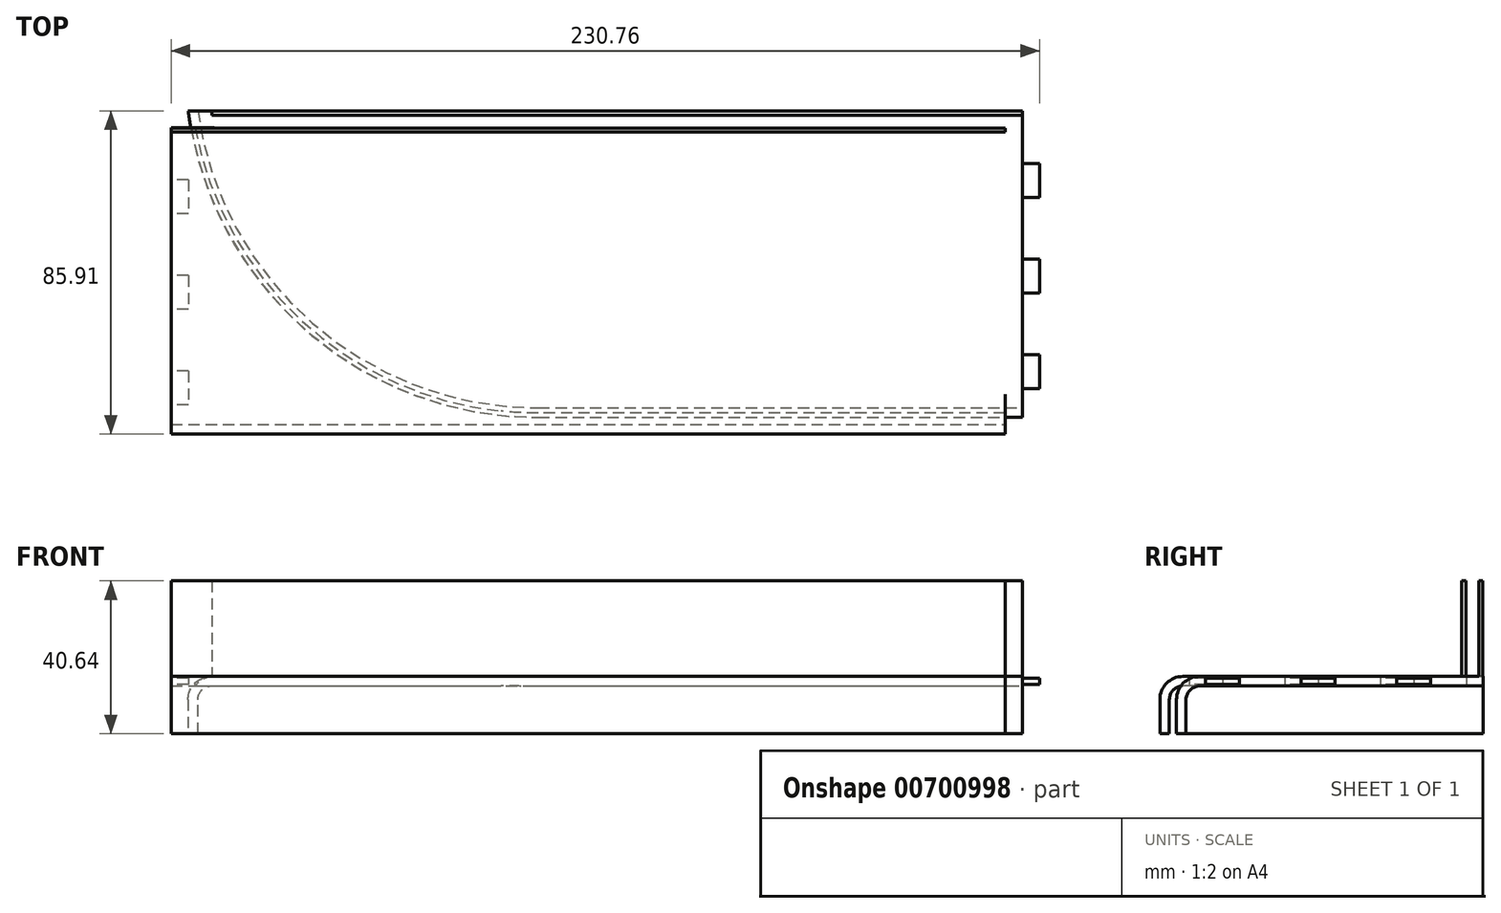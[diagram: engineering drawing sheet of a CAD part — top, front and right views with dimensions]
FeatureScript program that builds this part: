
annotation { "Feature Type Name" : "Feature", "Feature Type Description" : "" }
export const myFeature = defineFeature(function(context is Context, id is Id, definition is map)
    precondition{}
    {
        {
            var Q0;
            Q0=qCreatedBy(makeId("Top.planeOp"),FACE);
            var sketch = newSketch(context, id + "F0", { "sketchPlane" : qUnion([Q0])});
            skLineSegment(sketch, "E0.bottom", {"start": v(-106.27, 45.17) * mm, "end": v(115.37, 45.17) * mm});
            skLineSegment(sketch, "E0.top", {"start": v(-106.27, -36.31) * mm, "end": v(115.37, -36.31) * mm});
            skLineSegment(sketch, "E0.left", {"start": v(-106.27, 45.17) * mm, "end": v(-106.27, -36.31) * mm});
            skLineSegment(sketch, "E0.right", {"start": v(115.37, 45.17) * mm, "end": v(115.37, -36.31) * mm});
            skSolve(sketch);
        }
        {
            var Q0;
            Q0 = qSketchRegion(id + "F0", true);
            extrude(context, id + "F1", {"entities" : qUnion([Q0]), "depth" : 15.24 * mm, "offsetDistance" : 25.4 * mm});
        }
        {
            var Q0;
            Q0=makeQuery(id+"F1.opExtrude","SWEPT_EDGE",EDGE,{"disambiguationData":[OSD([sQuery(id+"F0.wireOp",EDGE,"E0.top"),sQuery(id+"F0.wireOp",EDGE,"E0.left")])]});
            fillet(context, id + "F2", {"entities" : qUnion([Q0]), "radius" : 93.82 * mm, "tangentPropagation" : true, "allowEdgeOverflow" : false});
        }
        {
            var Q0;
            {var subQ0=sQuery(id+"F0.wireOp",EDGE,"E0.left");var subQ1=sQuery(id+"F0.wireOp",EDGE,"E0.bottom");Q0=makeQuery(id+"F2.opFillet","BLEND_EDGE",EDGE,{"blendedFrom":[makeQuery(id+"F1.opExtrude","SWEPT_EDGE",EDGE,{"disambiguationData":[OSD([subQ1,subQ0])]}),makeQuery(id+"F1.opExtrude","CAP_FACE",FACE,{"disambiguationData":[OSD([subQ1,sQuery(id+"F0.wireOp",EDGE,"E0.top"),subQ0,sQuery(id+"F0.wireOp",EDGE,"E0.right")])],"isStart":false})],"blendedInto":[makeQuery(id+"F1.opExtrude","CAP_FACE",FACE,{"disambiguationData":[OSD([subQ1,sQuery(id+"F0.wireOp",EDGE,"E0.top"),subQ0,sQuery(id+"F0.wireOp",EDGE,"E0.right")])],"isStart":false})]});}
            var Q1;
            Q1=makeQuery(id+"F1.opExtrude","CAP_EDGE",EDGE,{"disambiguationData":[OSD([sQuery(id+"F0.wireOp",EDGE,"E0.top")])],"isStart":false});
            fillet(context, id + "F3", {"entities" : qUnion([Q0, Q1]), "radius" : 6.13 * mm, "tangentPropagation" : true, "allowEdgeOverflow" : false});
        }
        {
            var Q0;
            Q0=makeQuery(id+"F1.opExtrude","CAP_FACE",FACE,{"disambiguationData":[OSD([sQuery(id+"F0.wireOp",EDGE,"E0.bottom"),sQuery(id+"F0.wireOp",EDGE,"E0.top"),sQuery(id+"F0.wireOp",EDGE,"E0.left"),sQuery(id+"F0.wireOp",EDGE,"E0.right")])],"isStart":true});
            var Q1;
            Q1=makeQuery(id+"F1.opExtrude","SWEPT_FACE",FACE,{"disambiguationData":[OSD([sQuery(id+"F0.wireOp",EDGE,"E0.bottom")])]});
            var Q2;
            Q2=makeQuery(id+"F1.opExtrude","SWEPT_FACE",FACE,{"disambiguationData":[OSD([sQuery(id+"F0.wireOp",EDGE,"E0.right")])]});
            shell(context, id + "F4", {"entities" : qUnion([Q0, Q1, Q2]), "thickness" : 2.54 * mm});
        }
        {
            var Q0;
            Q0=makeQuery(id+"F1.opExtrude","SWEPT_FACE",FACE,{"disambiguationData":[OSD([sQuery(id+"F0.wireOp",EDGE,"E0.right")])]});
            var sketch = newSketch(context, id + "F5", { "sketchPlane" : qUnion([Q0])});
            skLineSegment(sketch, "E1.bottom", {"start": v(-29.1, 15.24) * mm, "end": v(-19.17, 15.24) * mm});
            skLineSegment(sketch, "E1.top", {"start": v(-29.1, 12.7) * mm, "end": v(-19.17, 12.7) * mm});
            skLineSegment(sketch, "E1.left", {"start": v(-29.1, 15.24) * mm, "end": v(-29.1, 12.7) * mm});
            skLineSegment(sketch, "E1.right", {"start": v(-19.17, 15.24) * mm, "end": v(-19.17, 12.7) * mm});
            skLineSegment(sketch, "E2.1.0.0", {"start": v(-3.7, 15.24) * mm, "end": v(-3.7, 12.7) * mm});
            skLineSegment(sketch, "E2.1.0.1", {"start": v(-3.7, 15.24) * mm, "end": v(6.23, 15.24) * mm});
            skLineSegment(sketch, "E2.1.0.2", {"start": v(-3.7, 12.7) * mm, "end": v(6.23, 12.7) * mm});
            skLineSegment(sketch, "E2.1.0.3", {"start": v(6.23, 15.24) * mm, "end": v(6.23, 12.7) * mm});
            skLineSegment(sketch, "E2.2.0.0", {"start": v(21.7, 15.24) * mm, "end": v(21.7, 12.7) * mm});
            skLineSegment(sketch, "E2.2.0.1", {"start": v(21.7, 15.24) * mm, "end": v(31.63, 15.24) * mm});
            skLineSegment(sketch, "E2.2.0.2", {"start": v(21.7, 12.7) * mm, "end": v(31.63, 12.7) * mm});
            skLineSegment(sketch, "E2.2.0.3", {"start": v(31.63, 15.24) * mm, "end": v(31.63, 12.7) * mm});
            skLineSegment(sketch, "E2.direction1", {"start": v(-29.1, 12.7) * mm, "end": v(-3.7, 12.7) * mm, "construction": true});
            skLineSegment(sketch, "E3.0", {"start": v(-28.6, 14.76) * mm, "end": v(-28.6, 13.18) * mm});
            skLineSegment(sketch, "E3.1", {"start": v(-28.6, 14.76) * mm, "end": v(-19.65, 14.76) * mm});
            skLineSegment(sketch, "E3.2", {"start": v(-19.65, 14.76) * mm, "end": v(-19.65, 13.18) * mm});
            skLineSegment(sketch, "E3.3", {"start": v(-28.6, 13.18) * mm, "end": v(-19.65, 13.18) * mm});
            skLineSegment(sketch, "E4.0", {"start": v(-3.2, 14.76) * mm, "end": v(5.75, 14.76) * mm});
            skLineSegment(sketch, "E4.1", {"start": v(-3.2, 14.76) * mm, "end": v(-3.2, 13.18) * mm});
            skLineSegment(sketch, "E4.2", {"start": v(-3.2, 13.18) * mm, "end": v(5.75, 13.18) * mm});
            skLineSegment(sketch, "E4.3", {"start": v(5.75, 14.76) * mm, "end": v(5.75, 13.18) * mm});
            skLineSegment(sketch, "E5.0", {"start": v(22.2, 14.76) * mm, "end": v(22.2, 13.18) * mm});
            skLineSegment(sketch, "E5.1", {"start": v(22.2, 14.76) * mm, "end": v(31.15, 14.76) * mm});
            skLineSegment(sketch, "E5.2", {"start": v(31.15, 14.76) * mm, "end": v(31.15, 13.18) * mm});
            skLineSegment(sketch, "E5.3", {"start": v(22.2, 13.18) * mm, "end": v(31.15, 13.18) * mm});
            skSolve(sketch);
        }
        {
            var Q0;
            Q0=makeQuery(id+"F5.imprint","IMPRINT",FACE,{"disambiguationData":[TD([[makeQuery(id+"F5.imprint","IMPRINT",EDGE,{"derivedFrom":sQuery(id+"F5.wireOp",EDGE,"E3.0")}),1.0]])]});
            var Q1;
            Q1=makeQuery(id+"F5.imprint","IMPRINT",FACE,{"disambiguationData":[TD([[makeQuery(id+"F5.imprint","IMPRINT",EDGE,{"derivedFrom":sQuery(id+"F5.wireOp",EDGE,"E4.0")}),-1.0]])]});
            var Q2;
            Q2=makeQuery(id+"F5.imprint","IMPRINT",FACE,{"disambiguationData":[TD([[makeQuery(id+"F5.imprint","IMPRINT",EDGE,{"derivedFrom":sQuery(id+"F5.wireOp",EDGE,"E5.0")}),1.0]])]});
            extrude(context, id + "F6", {"entities" : qUnion([Q0, Q1, Q2]), "operationType" : NewBodyOperationType.ADD, "depth" : 4.57 * mm, "offsetDistance" : 25.4 * mm});
        }
        {
            var Q0;
            Q0=qCreatedBy(makeId("Top.planeOp"),FACE);
            var sketch = newSketch(context, id + "F7", { "sketchPlane" : qUnion([Q0])});
            skLineSegment(sketch, "E6.bottom", {"start": v(-110.82, 40.74) * mm, "end": v(110.82, 40.74) * mm});
            skLineSegment(sketch, "E6.top", {"start": v(-110.82, -40.74) * mm, "end": v(110.82, -40.74) * mm});
            skLineSegment(sketch, "E6.left", {"start": v(-110.82, 40.74) * mm, "end": v(-110.82, -40.74) * mm});
            skLineSegment(sketch, "E6.right", {"start": v(110.82, 40.74) * mm, "end": v(110.82, -40.74) * mm});
            skSolve(sketch);
        }
        {
            var Q0;
            Q0 = qSketchRegion(id + "F7", true);
            extrude(context, id + "F8", {"entities" : qUnion([Q0]), "depth" : 15.24 * mm, "offsetDistance" : 25.4 * mm});
        }
        {
            var Q0;
            Q0=makeQuery(id+"F8.opExtrude","CAP_EDGE",EDGE,{"disambiguationData":[OSD([sQuery(id+"F7.wireOp",EDGE,"E6.top")])],"isStart":false});
            fillet(context, id + "F9", {"entities" : qUnion([Q0]), "radius" : 6.12 * mm, "tangentPropagation" : true, "allowEdgeOverflow" : false});
        }
        {
            var Q0;
            Q0=makeQuery(id+"F8.opExtrude","CAP_FACE",FACE,{"disambiguationData":[OSD([sQuery(id+"F7.wireOp",EDGE,"E6.bottom"),sQuery(id+"F7.wireOp",EDGE,"E6.top"),sQuery(id+"F7.wireOp",EDGE,"E6.left"),sQuery(id+"F7.wireOp",EDGE,"E6.right")])],"isStart":true});
            var Q1;
            Q1=makeQuery(id+"F8.opExtrude","SWEPT_FACE",FACE,{"disambiguationData":[OSD([sQuery(id+"F7.wireOp",EDGE,"E6.left")])]});
            var Q2;
            Q2=makeQuery(id+"F8.opExtrude","SWEPT_FACE",FACE,{"disambiguationData":[OSD([sQuery(id+"F7.wireOp",EDGE,"E6.right")])]});
            var Q3;
            Q3=makeQuery(id+"F8.opExtrude","SWEPT_FACE",FACE,{"disambiguationData":[OSD([sQuery(id+"F7.wireOp",EDGE,"E6.bottom")])]});
            shell(context, id + "F10", {"entities" : qUnion([Q0, Q1, Q2, Q3]), "thickness" : 2.54 * mm});
        }
        {
            var Q0;
            Q0=makeQuery(id+"F8.opExtrude","SWEPT_FACE",FACE,{"disambiguationData":[OSD([sQuery(id+"F7.wireOp",EDGE,"E6.left")])]});
            var sketch = newSketch(context, id + "F11", { "sketchPlane" : qUnion([Q0])});
            skLineSegment(sketch, "E7.bottom", {"start": v(-27.3, 15.23) * mm, "end": v(-17.37, 15.23) * mm});
            skLineSegment(sketch, "E7.top", {"start": v(-27.3, 12.7) * mm, "end": v(-17.37, 12.7) * mm});
            skLineSegment(sketch, "E7.left", {"start": v(-27.3, 15.23) * mm, "end": v(-27.3, 12.7) * mm});
            skLineSegment(sketch, "E7.right", {"start": v(-17.37, 15.23) * mm, "end": v(-17.37, 12.7) * mm});
            skLineSegment(sketch, "E8.1.0.0", {"start": v(-1.9, 15.23) * mm, "end": v(-1.9, 12.7) * mm});
            skLineSegment(sketch, "E8.1.0.1", {"start": v(-1.9, 15.23) * mm, "end": v(8.03, 15.23) * mm});
            skLineSegment(sketch, "E8.1.0.2", {"start": v(-1.9, 12.7) * mm, "end": v(8.03, 12.7) * mm});
            skLineSegment(sketch, "E8.1.0.3", {"start": v(8.03, 15.23) * mm, "end": v(8.03, 12.7) * mm});
            skLineSegment(sketch, "E8.2.0.0", {"start": v(23.5, 15.23) * mm, "end": v(23.5, 12.7) * mm});
            skLineSegment(sketch, "E8.2.0.1", {"start": v(23.5, 15.23) * mm, "end": v(33.43, 15.23) * mm});
            skLineSegment(sketch, "E8.2.0.2", {"start": v(23.5, 12.7) * mm, "end": v(33.43, 12.7) * mm});
            skLineSegment(sketch, "E8.2.0.3", {"start": v(33.43, 15.23) * mm, "end": v(33.43, 12.7) * mm});
            skLineSegment(sketch, "E8.direction1", {"start": v(-27.3, 12.7) * mm, "end": v(-1.9, 12.7) * mm, "construction": true});
            skLineSegment(sketch, "E9.0", {"start": v(-26.81, 14.74) * mm, "end": v(-26.81, 13.18) * mm});
            skLineSegment(sketch, "E9.1", {"start": v(-26.81, 14.74) * mm, "end": v(-17.85, 14.74) * mm});
            skLineSegment(sketch, "E9.2", {"start": v(-17.85, 14.74) * mm, "end": v(-17.85, 13.18) * mm});
            skLineSegment(sketch, "E9.3", {"start": v(-26.81, 13.18) * mm, "end": v(-17.85, 13.18) * mm});
            skLineSegment(sketch, "E10.0", {"start": v(-1.41, 14.74) * mm, "end": v(7.55, 14.74) * mm});
            skLineSegment(sketch, "E10.1", {"start": v(-1.41, 14.74) * mm, "end": v(-1.41, 13.18) * mm});
            skLineSegment(sketch, "E10.2", {"start": v(-1.41, 13.18) * mm, "end": v(7.55, 13.18) * mm});
            skLineSegment(sketch, "E10.3", {"start": v(7.55, 14.74) * mm, "end": v(7.55, 13.18) * mm});
            skLineSegment(sketch, "E11.0", {"start": v(23.99, 14.74) * mm, "end": v(23.99, 13.18) * mm});
            skLineSegment(sketch, "E11.1", {"start": v(23.99, 14.74) * mm, "end": v(32.95, 14.74) * mm});
            skLineSegment(sketch, "E11.2", {"start": v(32.95, 14.74) * mm, "end": v(32.95, 13.18) * mm});
            skLineSegment(sketch, "E11.3", {"start": v(23.99, 13.18) * mm, "end": v(32.95, 13.18) * mm});
            skSolve(sketch);
        }
        {
            var Q0;
            Q0=makeQuery(id+"F11.imprint","IMPRINT",FACE,{"disambiguationData":[TD([[makeQuery(id+"F11.imprint","IMPRINT",EDGE,{"derivedFrom":sQuery(id+"F11.wireOp",EDGE,"E9.0")}),1.0]])]});
            var Q1;
            Q1=makeQuery(id+"F11.imprint","IMPRINT",FACE,{"disambiguationData":[TD([[makeQuery(id+"F11.imprint","IMPRINT",EDGE,{"derivedFrom":sQuery(id+"F11.wireOp",EDGE,"E10.0")}),-1.0]])]});
            var Q2;
            Q2=makeQuery(id+"F11.imprint","IMPRINT",FACE,{"disambiguationData":[TD([[makeQuery(id+"F11.imprint","IMPRINT",EDGE,{"derivedFrom":sQuery(id+"F11.wireOp",EDGE,"E11.0")}),1.0]])]});
            extrude(context, id + "F12", {"entities" : qUnion([Q0, Q1, Q2]), "operationType" : NewBodyOperationType.REMOVE, "oppositeDirection" : true, "depth" : 4.57 * mm, "offsetDistance" : 25.4 * mm});
        }
        {
            var Q0;
            Q0=makeQuery(id+"F1.opExtrude","CAP_FACE",FACE,{"disambiguationData":[OSD([sQuery(id+"F0.wireOp",EDGE,"E0.bottom"),sQuery(id+"F0.wireOp",EDGE,"E0.top"),sQuery(id+"F0.wireOp",EDGE,"E0.left"),sQuery(id+"F0.wireOp",EDGE,"E0.right")])],"isStart":false});
            var sketch = newSketch(context, id + "F13", { "sketchPlane" : qUnion([Q0])});
            skLineSegment(sketch, "E12.bottom", {"start": v(115.37, 43.98) * mm, "end": v(-100, 43.98) * mm});
            skLineSegment(sketch, "E12.top", {"start": v(115.37, 45.1) * mm, "end": v(-100, 45.1) * mm});
            skLineSegment(sketch, "E12.left", {"start": v(115.37, 43.98) * mm, "end": v(115.37, 45.1) * mm});
            skLineSegment(sketch, "E12.right", {"start": v(-100, 43.98) * mm, "end": v(-100, 45.1) * mm});
            skSolve(sketch);
        }
        {
            var Q0;
            Q0 = qSketchRegion(id + "F13", true);
            extrude(context, id + "F14", {"entities" : qUnion([Q0]), "operationType" : NewBodyOperationType.ADD, "depth" : 25.4 * mm, "offsetDistance" : 25.4 * mm});
        }
        {
            var Q0;
            Q0=makeQuery(id+"F8.opExtrude","CAP_FACE",FACE,{"disambiguationData":[OSD([sQuery(id+"F7.wireOp",EDGE,"E6.bottom"),sQuery(id+"F7.wireOp",EDGE,"E6.top"),sQuery(id+"F7.wireOp",EDGE,"E6.left"),sQuery(id+"F7.wireOp",EDGE,"E6.right")])],"isStart":false});
            var sketch = newSketch(context, id + "F15", { "sketchPlane" : qUnion([Q0])});
            skLineSegment(sketch, "E13.bottom", {"start": v(110.82, 39.5) * mm, "end": v(-110.82, 39.5) * mm});
            skLineSegment(sketch, "E13.top", {"start": v(110.82, 40.62) * mm, "end": v(-110.82, 40.62) * mm});
            skLineSegment(sketch, "E13.left", {"start": v(110.82, 39.5) * mm, "end": v(110.82, 40.62) * mm});
            skLineSegment(sketch, "E13.right", {"start": v(-110.82, 39.5) * mm, "end": v(-110.82, 40.62) * mm});
            skSolve(sketch);
        }
        {
            var Q0;
            Q0 = qSketchRegion(id + "F15", true);
            extrude(context, id + "F16", {"entities" : qUnion([Q0]), "operationType" : NewBodyOperationType.ADD, "depth" : 25.4 * mm, "offsetDistance" : 25.4 * mm});
        }
    });
